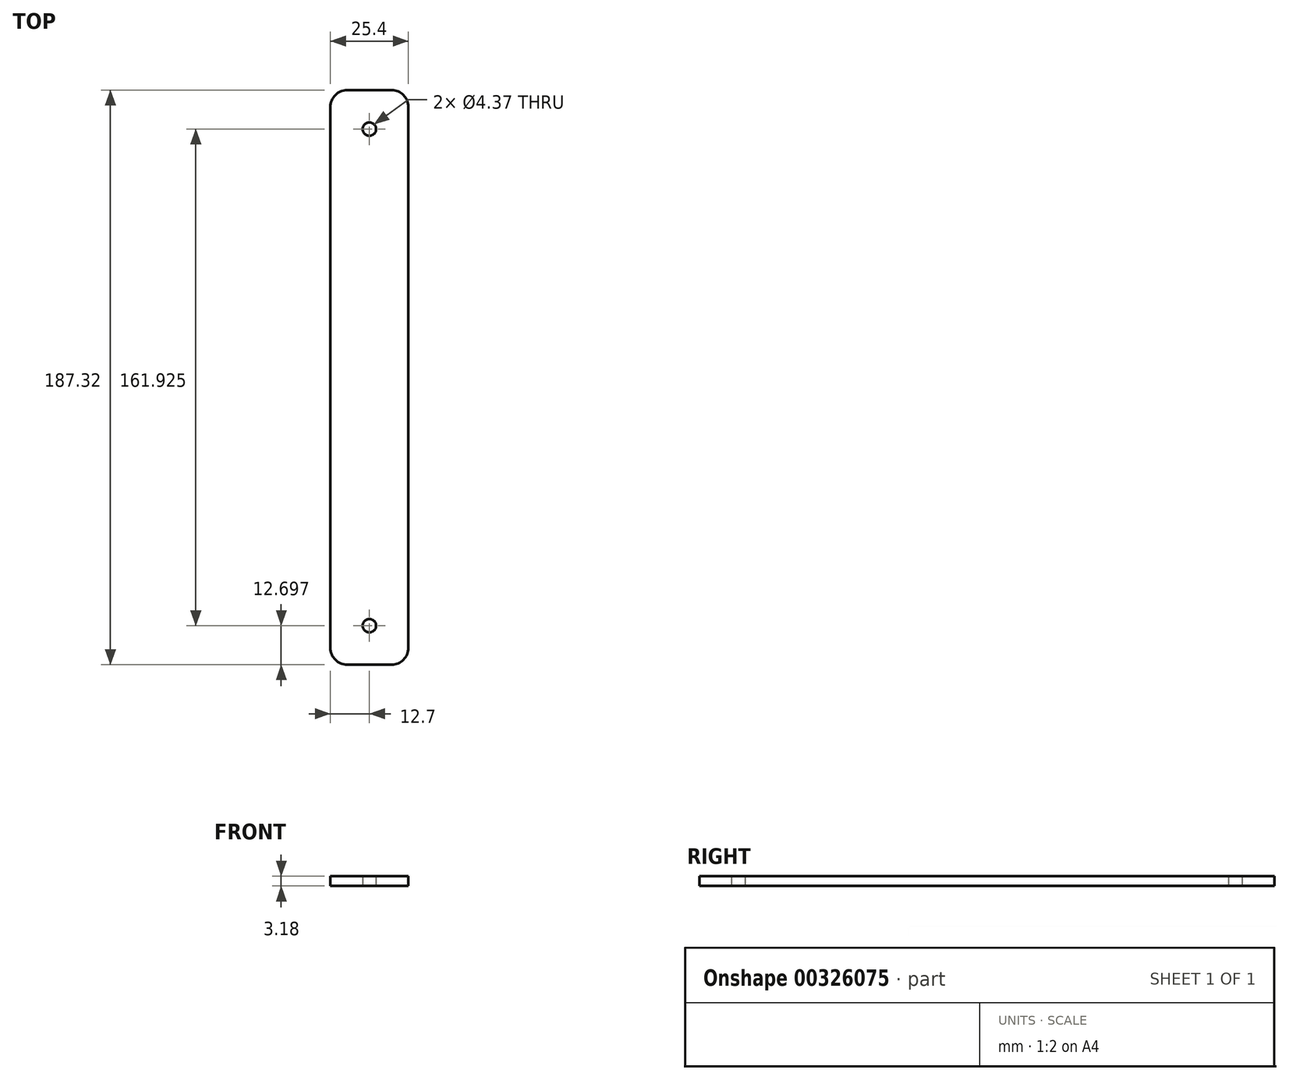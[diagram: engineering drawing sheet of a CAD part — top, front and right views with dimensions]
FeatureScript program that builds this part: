
annotation { "Feature Type Name" : "Feature", "Feature Type Description" : "" }
export const myFeature = defineFeature(function(context is Context, id is Id, definition is map)
    precondition{}
    {
        {
            var Q0;
            Q0=qCreatedBy(makeId("Top.planeOp"),FACE);
            var sketch = newSketch(context, id + "F0", { "sketchPlane" : qUnion([Q0])});
            skLineSegment(sketch, "E0.bottom", {"start": v(-7.24, 93.66) * mm, "end": v(7.24, 93.66) * mm});
            skLineSegment(sketch, "E0.top", {"start": v(-7.24, -93.66) * mm, "end": v(7.24, -93.66) * mm});
            skLineSegment(sketch, "E0.left", {"start": v(-12.7, 88.2) * mm, "end": v(-12.7, -88.2) * mm});
            skLineSegment(sketch, "E0.right", {"start": v(12.7, 88.2) * mm, "end": v(12.7, -88.2) * mm});
            skPoint(sketch, "E0.middle", {"position": v(0, 0) * mm});
            skPoint(sketch, "E1.visualSharp", {"position": v(-12.7, 93.66) * mm});
            skArc(sketch, "E1.filletArc", {"start": v(-7.24, 93.66) * mm, "mid": v(-11.1, 92.06) * mm, "end": v(-12.7, 88.2) * mm});
            skPoint(sketch, "E2.visualSharp", {"position": v(12.7, 93.66) * mm});
            skArc(sketch, "E2.filletArc", {"start": v(12.7, 88.2) * mm, "mid": v(11.1, 92.06) * mm, "end": v(7.24, 93.66) * mm});
            skPoint(sketch, "E3.visualSharp", {"position": v(12.7, -93.66) * mm});
            skArc(sketch, "E3.filletArc", {"start": v(7.24, -93.66) * mm, "mid": v(11.1, -92.06) * mm, "end": v(12.7, -88.2) * mm});
            skPoint(sketch, "E4.visualSharp", {"position": v(-12.7, -93.66) * mm});
            skArc(sketch, "E4.filletArc", {"start": v(-12.7, -88.2) * mm, "mid": v(-11.1, -92.06) * mm, "end": v(-7.24, -93.66) * mm});
            skCircle(sketch, "E5", {"center": v(0, 80.96) * mm, "radius": 2.18 * mm});
            skCircle(sketch, "E6", {"center": v(0, -80.96) * mm, "radius": 2.18 * mm});
            skLineSegment(sketch, "E7.MirrorCS", {"start": v(12.7, -88.2) * mm, "end": v(12.7, 88.2) * mm});
            skSolve(sketch);
        }
        {
            var Q0;
            Q0 = qSketchRegion(id + "F0", true);
            extrude(context, id + "F1", {"entities" : qUnion([Q0]), "depth" : 3.17 * mm});
        }
    });
